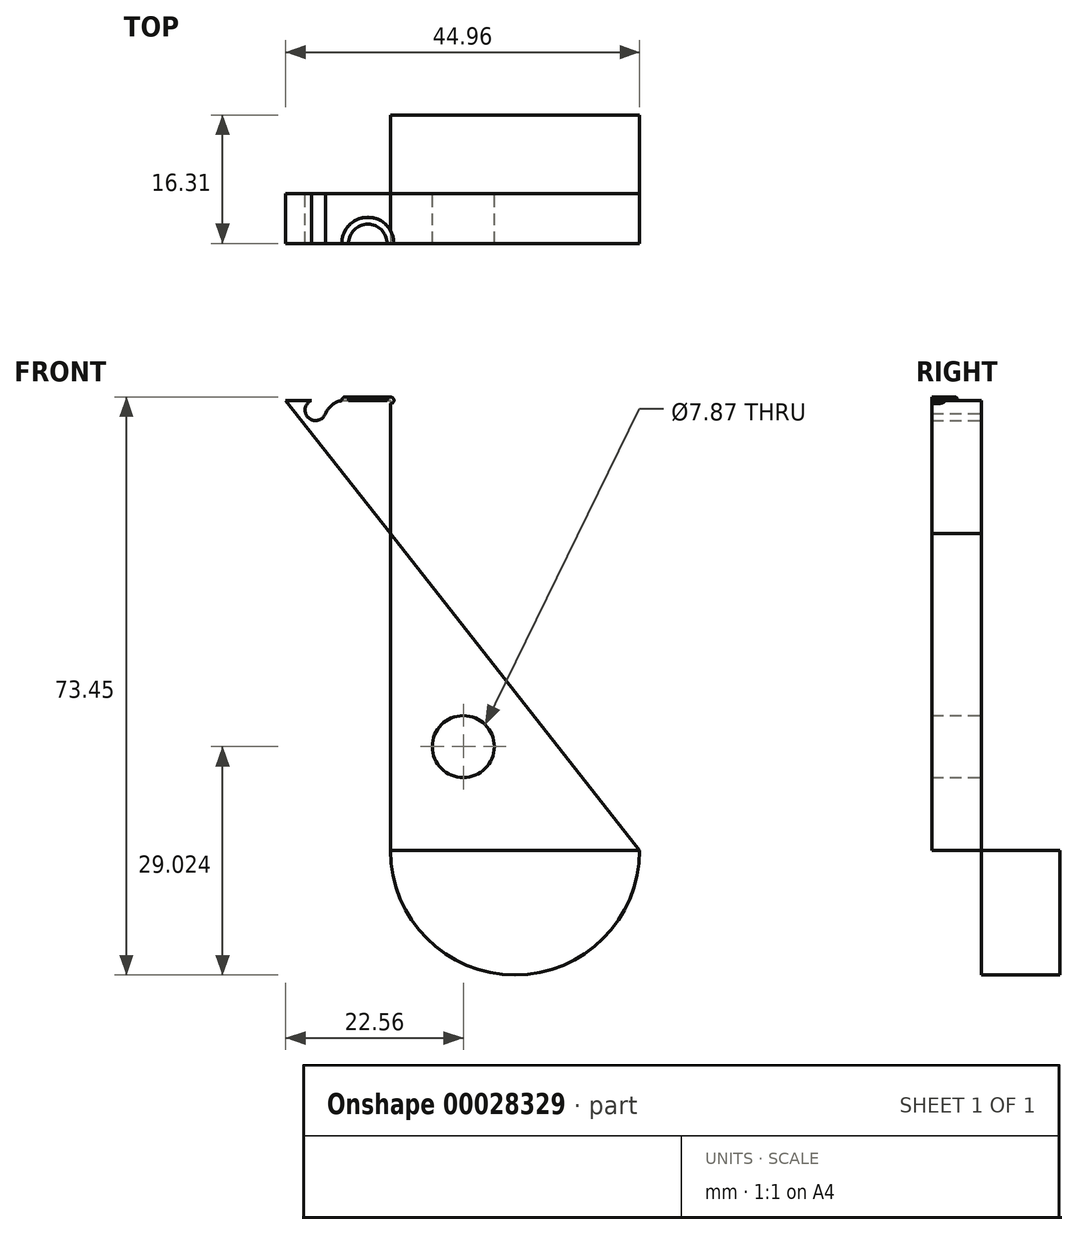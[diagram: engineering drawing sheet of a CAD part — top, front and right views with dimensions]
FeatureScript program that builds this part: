
annotation { "Feature Type Name" : "Feature", "Feature Type Description" : "" }
export const myFeature = defineFeature(function(context is Context, id is Id, definition is map)
    precondition{}
    {
        {
            var Q0;
            Q0=qCreatedBy(makeId("Front.planeOp"),FACE);
            var sketch = newSketch(context, id + "F0", { "sketchPlane" : qUnion([Q0])});
            skLineSegment(sketch, "E0", {"start": v(-8.3, -38.22) * mm, "end": v(23.35, -38.22) * mm});
            skLineSegment(sketch, "E1", {"start": v(23.35, -38.22) * mm, "end": v(-21.6, 18.96) * mm});
            skLineSegment(sketch, "E2", {"start": v(-8.3, 18.96) * mm, "end": v(-21.6, 18.96) * mm});
            skLineSegment(sketch, "E3", {"start": v(-8.3, -38.22) * mm, "end": v(-8.3, 18.96) * mm});
            skCircle(sketch, "E4", {"center": v(0.95, -25.03) * mm, "radius": 3.93 * mm});
            skCircle(sketch, "E5", {"center": v(-14.05, 16.25) * mm, "radius": 2.7 * mm});
            skPoint(sketch, "E5.first.point", {"position": v(-15.83, 18.29) * mm});
            skPoint(sketch, "E5.second.point", {"position": v(-11.5, 15.33) * mm});
            skPoint(sketch, "E5.third.point", {"position": v(-16.56, 17.27) * mm});
            skCircle(sketch, "E6", {"center": v(-17.81, 17.73) * mm, "radius": 1.34 * mm});
            skPoint(sketch, "E6.second.point", {"position": v(-18.46, 18.9) * mm});
            skPoint(sketch, "E6.third.point", {"position": v(-16.56, 18.2) * mm});
            skEllipse(sketch, "E7", {"center": v(-39.32, 15.94) * mm, "majorRadius": 6.45 * mm, "minorRadius": 1.06 * mm, "majorAxis": v(1, -0.1)});
            skArc(sketch, "E8", {"start": v(-8.3, -38.22) * mm, "mid": v(7.52, -54.05) * mm, "end": v(23.35, -38.22) * mm});
            skSolve(sketch);
        }
        {
            var Q0;
            {var subQ1=sQuery(id+"F0.wireOp",EDGE,"E5");var subQ4=makeQuery(id+"F0.imprint","INTERSECT",VERTEX,{"derivedFrom":[sQuery(id+"F0.wireOp",EDGE,"E2"),subQ1]});Q0=makeQuery(id+"F0.imprint","IMPRINT",FACE,{"disambiguationData":[TD([[makeQuery(id+"F0.imprint","IMPRINT",EDGE,{"disambiguationData":[TD([[subQ4,-1.0]])],"derivedFrom":subQ1}),1.0]])]});}
            var Q1;
            {var subQ3=sQuery(id+"F0.wireOp",EDGE,"E2");var subQ6=sQuery(id+"F0.wireOp",EDGE,"E1");var subQ9=makeQuery(id+"F0.imprint","INTERSECT",VERTEX,{"derivedFrom":[subQ6,subQ3]});Q1=makeQuery(id+"F0.imprint","IMPRINT",FACE,{"disambiguationData":[TD([[makeQuery(id+"F0.imprint","IMPRINT",EDGE,{"disambiguationData":[TD([[subQ9,1.0]])],"derivedFrom":subQ6}),-1.0]])]});}
            var Q2;
            {var subQ3=sQuery(id+"F0.wireOp",EDGE,"E0");Q2=makeQuery(id+"F0.imprint","IMPRINT",FACE,{"disambiguationData":[TD([[makeQuery(id+"F0.imprint","IMPRINT",EDGE,{"derivedFrom":subQ3}),1.0]])]});}
            extrude(context, id + "F1", {"entities" : qUnion([Q0, Q1, Q2]), "depth" : 6.34 * mm});
        }
        {
            var Q0;
            Q0=makeQuery(id+"F0.imprint","IMPRINT",FACE,{"disambiguationData":[TD([[makeQuery(id+"F0.imprint","IMPRINT",EDGE,{"derivedFrom":sQuery(id+"F0.wireOp",EDGE,"E0")}),-1.0]])]});
            extrude(context, id + "F2", {"entities" : qUnion([Q0]), "operationType" : NewBodyOperationType.ADD, "oppositeDirection" : true, "depth" : 9.97 * mm});
        }
        {
            var Q0;
            {var subQ0=sQuery(id+"F0.wireOp",EDGE,"E2");Q0=makeQuery(id+"F1.opExtrude","SWEPT_FACE",FACE,{"disambiguationData":[OSD([subQ0]),TDD([makeQuery(id+"F0.imprint","IMPRINT",EDGE,{"disambiguationData":[TD([[makeQuery(id+"F0.imprint","INTERSECT",VERTEX,{"derivedFrom":[subQ0,sQuery(id+"F0.wireOp",EDGE,"E3")]}),-1.0]])],"derivedFrom":subQ0})])]});}
            var sketch = newSketch(context, id + "F3", { "sketchPlane" : qUnion([Q0])});
            skArc(sketch, "E9", {"start": v(-8.3, -6.34) * mm, "mid": v(-11.18, -3.46) * mm, "end": v(-14.05, -6.34) * mm});
            skSolve(sketch);
        }
        {
            var Q0;
            Q0=makeQuery(id+"F1.opExtrude","CAP_FACE",FACE,{"disambiguationData":[OSD([sQuery(id+"F0.wireOp",EDGE,"E1"),sQuery(id+"F0.wireOp",EDGE,"E2"),sQuery(id+"F0.wireOp",EDGE,"E3"),sQuery(id+"F0.wireOp",EDGE,"E5"),sQuery(id+"F0.wireOp",EDGE,"E6")])],"isStart":false});
            var sketch = newSketch(context, id + "F4", { "sketchPlane" : qUnion([Q0])});
            skCircle(sketch, "E10", {"center": v(-14.05, 18.96) * mm, "radius": 0.44 * mm});
            skSolve(sketch);
        }
        {
            var Q0;
            Q0 = qSketchRegion(id + "F4", true);
            var Q1;
            Q1=sQuery(id+"F3.wireOp",EDGE,"E9");
            sweep(context, id + "F5", {"operationType" : NewBodyOperationType.ADD, "profiles" : qUnion([Q0]), "path" : qUnion([Q1])});
        }
    });
